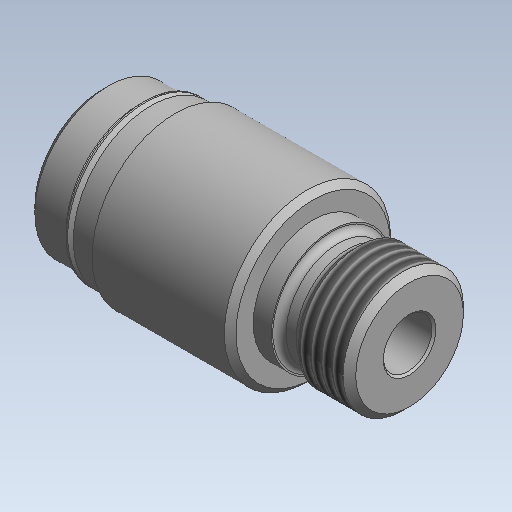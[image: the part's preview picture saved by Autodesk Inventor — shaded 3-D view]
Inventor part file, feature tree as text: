
AUTODESK INVENTOR PART (.ipt)
format: ipt  version: 2020 (Build 240168000, 168)  size: 288,768 bytes
history: native  units: mm (DEFAULTED — no unit token found)
features: other x119, sketch x6, revolve x5, thread x2, hole x1
ambient origin geometry x8: Origin, YZ Plane, XZ Plane, XY Plane, X Axis, Y Axis, Z Axis, Center Point
bodies: Solid1 (feature_tree)
feature tree (133):
  revolve  "Revolution1"  [1 undecoded]
  thread  "Thread1"  [1 undecoded]
  revolve  "Revolution2"  Angle=360.0deg
  hole  "Hole1"  [1 undecoded]
  revolve  "Revolution3"  [1 undecoded]
  revolve  "Revolution4"  [1 undecoded]
  thread  "Thread2"  [1 undecoded]
  revolve  "Revolution5"  [1 undecoded]
  other  "dp1_XY"
  other  "dp1_YZ"
  other  "dp1_ZX"
  other  "dp1_X"
  other  "dp1_Y"
  other  "dp1_Z"
  other  "dp1_Center"
  other  "dp2_XY"
  other  "dp2_YZ"
  other  "dp2_ZX"
  other  "dp2_X"
  other  "dp2_Y"
  other  "dp2_Z"
  other  "dp2_Center"
  other  "hh_XY"
  other  "hh_YZ"
  other  "hh_ZX"
  other  "hh_X"
  other  "hh_Y"
  other  "hh_Z"
  other  "hh_Center"
  other  "port_XY"
  other  "port_YZ"
  other  "port_ZX"
  other  "port_X"
  other  "port_Y"
  other  "port_Z"
  other  "port_Center"
  other  "rod_guide_XY"
  other  "rod_guide_YZ"
  other  "rod_guide_ZX"
  other  "rod_guide_X"
  other  "rod_guide_Y"
  other  "rod_guide_Z"
  other  "rod_guide_Center"
  other  "s1_XY"
  other  "s1_YZ"
  other  "s1_ZX"
  other  "s1_X"
  other  "s1_Y"
  other  "s1_Z"
  other  "s1_Center"
  other  "s2_XY"
  other  "s2_YZ"
  other  "s2_ZX"
  other  "s2_X"
  other  "s2_Y"
  other  "s2_Z"
  other  "s2_Center"
  other  "t1_XY"
  other  "t1_YZ"
  other  "t1_ZX"
  other  "t1_X"
  other  "t1_Y"
  other  "t1_Z"
  other  "t1_Center"
  other  "t111_XY"
  other  "t111_YZ"
  other  "t111_ZX"
  other  "t111_X"
  other  "t111_Y"
  other  "t111_Z"
  other  "t111_Center"
  other  "to_foot_bracket_XY"
  other  "to_foot_bracket_YZ"
  other  "to_foot_bracket_ZX"
  other  "to_foot_bracket_X"
  other  "to_foot_bracket_Y"
  other  "to_foot_bracket_Z"
  other  "to_foot_bracket_Center"
  other  "to_nut_XY"
  other  "to_nut_YZ"
  other  "to_nut_ZX"
  other  "to_nut_X"
  other  "to_nut_Y"
  other  "to_nut_Z"
  other  "to_nut_Center"
  other  "to_rod_XY"
  other  "to_rod_YZ"
  other  "to_rod_ZX"
  other  "to_rod_X"
  other  "to_rod_Y"
  other  "to_rod_Z"
  other  "to_rod_Center"
  other  "to_screw_XY"
  other  "to_screw_YZ"
  other  "to_screw_ZX"
  other  "to_screw_X"
  other  "to_screw_Y"
  other  "to_screw_Z"
  other  "to_screw_Center"
  other  "to_trunnion_brackets_XY"
  other  "to_trunnion_brackets_YZ"
  other  "to_trunnion_brackets_ZX"
  other  "to_trunnion_brackets_X"
  other  "to_trunnion_brackets_Y"
  other  "to_trunnion_brackets_Z"
  other  "to_trunnion_brackets_Center"
  other  "to_trunnion_brackets1_XY"
  other  "to_trunnion_brackets1_YZ"
  other  "to_trunnion_brackets1_ZX"
  other  "to_trunnion_brackets1_X"
  other  "to_trunnion_brackets1_Y"
  other  "to_trunnion_brackets1_Z"
  other  "to_trunnion_brackets1_Center"
  other  "to_trunnion_brackets2_XY"
  other  "to_trunnion_brackets2_YZ"
  other  "to_trunnion_brackets2_ZX"
  other  "to_trunnion_brackets2_X"
  other  "to_trunnion_brackets2_Y"
  other  "to_trunnion_brackets2_Z"
  other  "to_trunnion_brackets2_Center"
  other  "to_tube_XY"
  other  "to_tube_YZ"
  other  "to_tube_ZX"
  other  "to_tube_X"
  other  "to_tube_Y"
  other  "to_tube_Z"
  other  "to_tube_Center"
  sketch  "Sketch_2"  dims[d0=360.0deg d1=5.84212mm d2=0.0mm d3=360.0deg]
  sketch  "Sketch_3"  dims[d4=6.4389mm d5=6.0mm d6=6.9469mm d7=2.0mm d8=90.0deg d9=40.4876mm d10=0.0mm d11=360.0deg]
  sketch  "Sketch3"  dims[d12=360.0deg d13=3.17653mm d14=0.0mm]
  sketch  "Sketch_10"  dims[d15=360.0deg]
  sketch  "Sketch_43"  dims[d16=0.0mm d17=0.0mm d18=0.0mm d19=0.0mm d20=0.0mm]
  sketch  "Sketch_47"
note: 7 required parameter values undecoded (feature->parameter linkage not recoverable at this tier; creation-order binding heuristic only, values carry confidence <= 0.55)